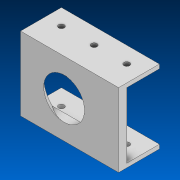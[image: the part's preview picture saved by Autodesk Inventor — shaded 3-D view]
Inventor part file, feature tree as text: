
AUTODESK INVENTOR PART (.ipt)
format: ipt  version: 2022.2 (Build 262287000, 287)  size: 145,408 bytes
history: native  units: in
note: dims shown in document units (in); Inventor stores cm internally (conversion verified against a paired STEP export)
features: sketch x4, extrude x3, chamfer x1, hole x1
ambient origin geometry x8: Origin, YZ Plane, XZ Plane, XY Plane, X Axis, Y Axis, Z Axis, Center Point
bodies: Solid1 (feature_tree)
feature tree (9):
  extrude  "Extrusion1"  Depth=1.25in
  chamfer  "Chamfer1"  Distance=1.0in
  extrude  "Extrusion2"  Depth=0.75in
  hole  "Hole1"  [1 undecoded]
  extrude  "Extrusion3"  Depth=0.75in TaperAngle=45.0deg
  sketch  "Sketch1"  dims[d0=1.25in d1=2.0in]
  sketch  "Sketch2"  dims[d3=0.168in]
  sketch  "Sketch3"  dims[d6=1.5in]
  sketch  "Sketch4"  dims[d7=1.5in d8=1.0in d9=1.0in d10=0.25in d11=0.0in d12=0.25in d13=0.25in d14=45.0deg d15=0.125in d16=1.0in d17=0.25in d18=0.0in d19=0.5in d20=1.0in d21=1.0in d22=0.5in d23=0.175in d24=0.75in d25=0.375in d26=0.25in d27=0.5635in d28=1.0in d29=0.8108in d30=1.0in d31=0.0in]
note: 1 required parameter value undecoded (feature->parameter linkage not recoverable at this tier; creation-order binding heuristic only, values carry confidence <= 0.55)
